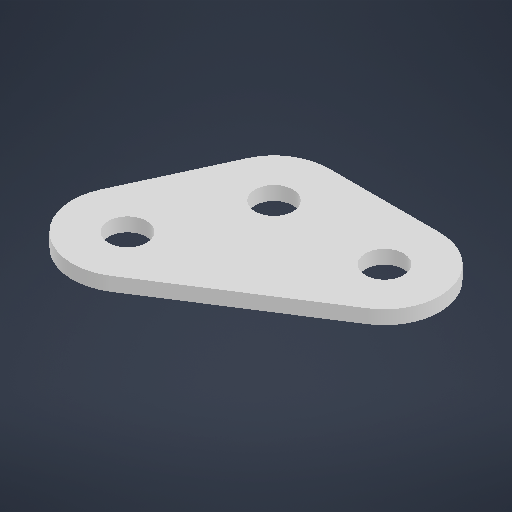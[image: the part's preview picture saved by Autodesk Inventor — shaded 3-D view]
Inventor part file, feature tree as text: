
AUTODESK INVENTOR PART (.ipt)
format: ipt  version: 2025.2 (Build 292293000, 293)  size: 190,464 bytes
history: native  units: in
note: dims shown in document units (in); Inventor stores cm internally (conversion verified against a paired STEP export)
features: extrude x1, sketch x1
ambient origin geometry x8: Origin, YZ Plane, XZ Plane, XY Plane, X Axis, Y Axis, Z Axis, Center Point
bodies: Solid1 (feature_tree)
feature tree (2):
  extrude  "Extrusion1"  Depth=0.0625in
  sketch  "Sketch1"  dims[d0=0.5in d1=0.5in d2=0.5in d3=0.0625in d4=0.0in]
